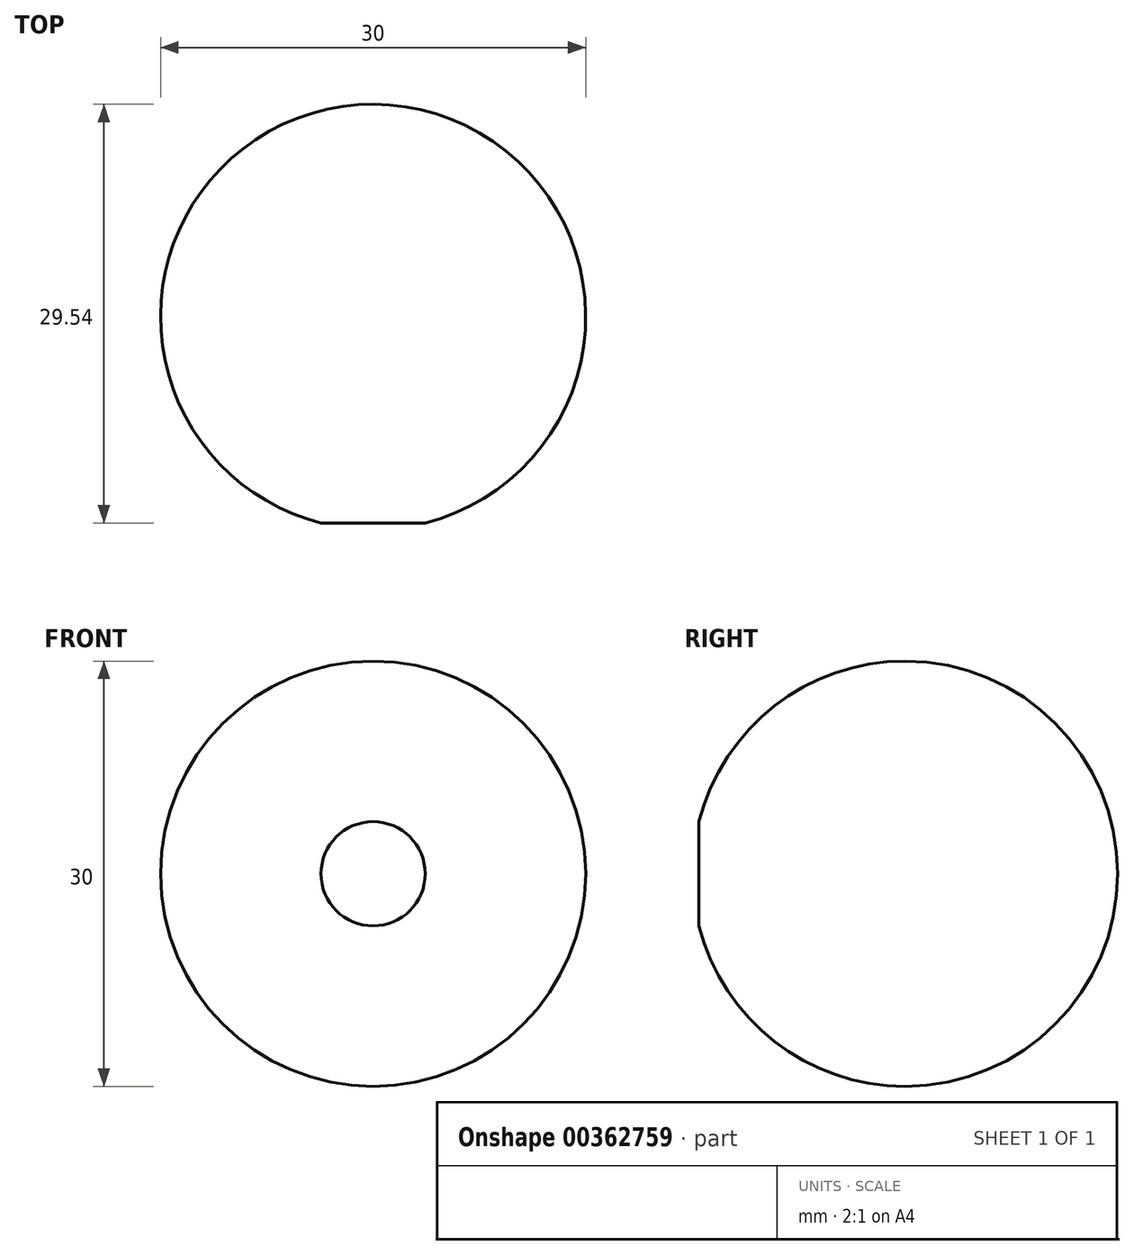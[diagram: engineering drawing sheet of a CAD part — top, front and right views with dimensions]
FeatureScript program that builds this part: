
annotation { "Feature Type Name" : "Feature", "Feature Type Description" : "" }
export const myFeature = defineFeature(function(context is Context, id is Id, definition is map)
    precondition{}
    {
        {
            var Q0;
            Q0=qCreatedBy(makeId("Front.planeOp"),FACE);
            var sketch = newSketch(context, id + "F0", { "sketchPlane" : qUnion([Q0])});
            skLineSegment(sketch, "E0.bottom", {"start": v(0, 0) * mm, "end": v(-30, 0) * mm});
            skLineSegment(sketch, "E0.top", {"start": v(0, 30) * mm, "end": v(-30, 30) * mm});
            skLineSegment(sketch, "E0.left", {"start": v(0, 0) * mm, "end": v(0, 30) * mm});
            skLineSegment(sketch, "E0.right", {"start": v(-30, 0) * mm, "end": v(-30, 30) * mm});
            skSolve(sketch);
        }
        {
            var Q0;
            Q0 = qSketchRegion(id + "F0", true);
            extrude(context, id + "F1", {"entities" : qUnion([Q0]), "depth" : 30 * mm});
        }
        {
            var Q0;
            Q0=makeQuery(id+"F1.opExtrude","CAP_FACE",FACE,{"disambiguationData":[OSD([sQuery(id+"F0.wireOp",EDGE,"E0.bottom"),sQuery(id+"F0.wireOp",EDGE,"E0.top"),sQuery(id+"F0.wireOp",EDGE,"E0.left"),sQuery(id+"F0.wireOp",EDGE,"E0.right")])],"isStart":false});
            var Q1;
            Q1=makeQuery(id+"F1.opExtrude","SWEPT_FACE",FACE,{"disambiguationData":[OSD([sQuery(id+"F0.wireOp",EDGE,"E0.top")])]});
            var Q2;
            Q2=makeQuery(id+"F1.opExtrude","SWEPT_FACE",FACE,{"disambiguationData":[OSD([sQuery(id+"F0.wireOp",EDGE,"E0.left")])]});
            var Q3;
            Q3=makeQuery(id+"F1.opExtrude","CAP_FACE",FACE,{"disambiguationData":[OSD([sQuery(id+"F0.wireOp",EDGE,"E0.bottom"),sQuery(id+"F0.wireOp",EDGE,"E0.top"),sQuery(id+"F0.wireOp",EDGE,"E0.left"),sQuery(id+"F0.wireOp",EDGE,"E0.right")])],"isStart":true});
            var Q4;
            Q4=makeQuery(id+"F1.opExtrude","SWEPT_FACE",FACE,{"disambiguationData":[OSD([sQuery(id+"F0.wireOp",EDGE,"E0.bottom")])]});
            fillet(context, id + "F2", {"entities" : qUnion([Q0, Q1, Q2, Q3, Q4]), "radius" : 15 * mm, "tangentPropagation" : true, "allowEdgeOverflow" : false});
        }
        {
            var Q0;
            Q0=qCreatedBy(makeId("Right.planeOp"),FACE);
            var sketch = newSketch(context, id + "F3", { "sketchPlane" : qUnion([Q0])});
            skLineSegment(sketch, "E1.bottom", {"start": v(-29.54, 26.73) * mm, "end": v(-31.54, 26.73) * mm});
            skLineSegment(sketch, "E1.top", {"start": v(-29.54, 0) * mm, "end": v(-31.54, 0) * mm});
            skLineSegment(sketch, "E1.left", {"start": v(-29.54, 26.73) * mm, "end": v(-29.54, 0) * mm});
            skLineSegment(sketch, "E1.right", {"start": v(-31.54, 26.73) * mm, "end": v(-31.54, 0) * mm});
            skSolve(sketch);
        }
        {
            var Q0;
            Q0 = qSketchRegion(id + "F3", true);
            extrude(context, id + "F4", {"entities" : qUnion([Q0]), "operationType" : NewBodyOperationType.REMOVE, "endBound" : BoundingType.THROUGH_ALL, "oppositeDirection" : true, "depth" : 25 * mm});
        }
    });
